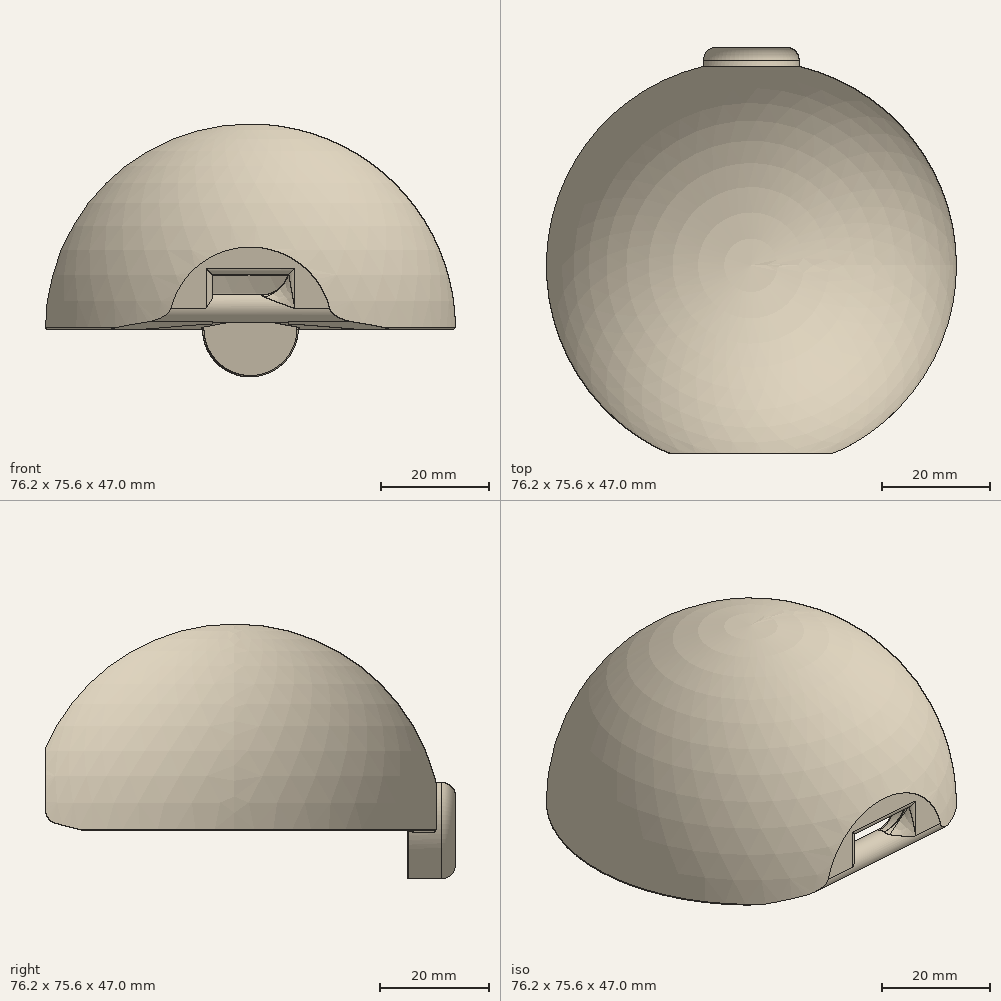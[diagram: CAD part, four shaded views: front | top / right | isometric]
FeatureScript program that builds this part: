
annotation { "Feature Type Name" : "Feature", "Feature Type Description" : "" }
export const myFeature = defineFeature(function(context is Context, id is Id, definition is map)
    precondition{}
    {
        {
            var Q0;
            Q0=qCreatedBy(makeId("Front.planeOp"),FACE);
            var sketch = newSketch(context, id + "F0", { "sketchPlane" : qUnion([Q0])});
            skArc(sketch, "E0", {"start": v(0, 38.1) * mm, "mid": v(-26.94, 26.94) * mm, "end": v(-38.1, 0) * mm});
            skLineSegment(sketch, "E1", {"start": v(-38.1, 0) * mm, "end": v(-31.75, 0) * mm});
            skArc(sketch, "E2.0", {"start": v(0, 31.75) * mm, "mid": v(-22.45, 22.45) * mm, "end": v(-31.75, 0) * mm});
            skLineSegment(sketch, "E3", {"start": v(0, 38.1) * mm, "end": v(0, 31.75) * mm});
            skSolve(sketch);
        }
        {
            var Q0;
            Q0=makeQuery(id+"F0.imprint","IMPRINT",FACE,{"disambiguationData":[TD([[makeQuery(id+"F0.imprint","IMPRINT",EDGE,{"derivedFrom":sQuery(id+"F0.wireOp",EDGE,"E0")}),1.0]])]});
            var Q1;
            Q1=sQuery(id+"F0.wireOp",EDGE,"E3");
            revolve(context, id + "F1", {"entities" : qUnion([Q0]), "axis" : qUnion([Q1]), "revolveType" : RevolveType.FULL});
        }
        {
            var Q0;
            Q0=qCreatedBy(makeId("Front.planeOp"),FACE);
            cPlane(context, id + "F2", {"entities" : qUnion([Q0]), "cplaneType" : CPlaneType.OFFSET, "offset" : 38.1 * mm, "oppositeDirection" : true, "width" : 152.4 * mm, "height" : 152.4 * mm});
        }
        {
            var Q0;
            Q0=qCreatedBy(id+"F2.planeOp",FACE);
            var sketch = newSketch(context, id + "F3", { "sketchPlane" : qUnion([Q0])});
            skCircle(sketch, "E4", {"center": v(0, 0) * mm, "radius": 8.9 * mm});
            skSolve(sketch);
        }
        {
            var Q0;
            Q0=makeQuery(id+"F3.imprint","IMPRINT",FACE,{"disambiguationData":[TD([[makeQuery(id+"F3.imprint","IMPRINT",EDGE,{"derivedFrom":sQuery(id+"F3.wireOp",EDGE,"E4")}),1.0]])]});
            extrude(context, id + "F4", {"entities" : qUnion([Q0]), "operationType" : NewBodyOperationType.ADD, "oppositeDirection" : true, "depth" : 2.54 * mm, "hasSecondDirection" : true, "secondDirectionOppositeDirection" : false, "secondDirectionDepth" : 6.35 * mm});
        }
        {
            var Q0;
            Q0=qCreatedBy(makeId("Right.planeOp"),FACE);
            var sketch = newSketch(context, id + "F5", { "sketchPlane" : qUnion([Q0])});
            skPoint(sketch, "E5.0.0.start.orphan", {"position": v(31.75, 0) * mm});
            skLineSegment(sketch, "E6.trimOffspring", {"start": v(-31.75, 0) * mm, "end": v(-38.1, 0) * mm});
            skPoint(sketch, "E5.0.1.start.orphan", {"position": v(37.05, 0) * mm});
            skPoint(sketch, "E5.0.4.end.orphan", {"position": v(31.75, 0) * mm});
            skPoint(sketch, "E5.0.2.end.orphan", {"position": v(37.05, 0) * mm});
            skPoint(sketch, "E5.0.2.start.orphan", {"position": v(31.75, 0) * mm});
            skCircle(sketch, "E7", {"center": v(-32.39, 3.81) * mm, "radius": 2.54 * mm});
            skLineSegment(sketch, "E8", {"start": v(-38.1, 0) * mm, "end": v(-38.1, 6.58) * mm});
            skLineSegment(sketch, "E9", {"start": v(-27.3, 0) * mm, "end": v(-38.1, 0) * mm});
            skArc(sketch, "E10", {"start": v(-27.3, 0) * mm, "mid": v(-29.08, 9.23) * mm, "end": v(-38.1, 6.58) * mm});
            skPoint(sketch, "E11.end.orphan", {"position": v(-21.82, 0) * mm});
            skSolve(sketch);
        }
        {
            var Q0;
            Q0=makeQuery(id+"F5.imprint","IMPRINT",FACE,{"disambiguationData":[TD([[makeQuery(id+"F5.imprint","IMPRINT",EDGE,{"derivedFrom":sQuery(id+"F5.wireOp",EDGE,"E7")}),-1.0]])]});
            extrude(context, id + "F6", {"entities" : qUnion([Q0]), "operationType" : NewBodyOperationType.REMOVE, "oppositeDirection" : true, "depth" : 13.97 * mm, "symmetric" : true});
        }
        {
            var Q0;
            Q0=qCreatedBy(makeId("Right.planeOp"),FACE);
            var sketch = newSketch(context, id + "F7", { "sketchPlane" : qUnion([Q0])});
            skCircle(sketch, "E12.0", {"center": v(-32.39, 3.81) * mm, "radius": 2.54 * mm});
            skLineSegment(sketch, "E13", {"start": v(-34.93, 3.81) * mm, "end": v(-34.93, 18.16) * mm});
            skLineSegment(sketch, "E14", {"start": v(-34.93, 18.16) * mm, "end": v(-42.82, 16.44) * mm});
            skLineSegment(sketch, "E15", {"start": v(-42.82, 16.44) * mm, "end": v(-48.56, -5.7) * mm});
            skLineSegment(sketch, "E16", {"start": v(-48.56, -5.7) * mm, "end": v(-6.3, -5.14) * mm});
            skLineSegment(sketch, "E17", {"start": v(-6.3, -5.14) * mm, "end": v(-27.81, 0) * mm});
            skLineSegment(sketch, "E18", {"start": v(-27.81, 0) * mm, "end": v(-33.02, 1.35) * mm});
            skSolve(sketch);
        }
        {
            var Q0;
            {var subQ0=sQuery(id+"F7.wireOp",EDGE,"E13");Q0=makeQuery(id+"F7.imprint","IMPRINT",FACE,{"disambiguationData":[TD([[makeQuery(id+"F7.imprint","IMPRINT",EDGE,{"derivedFrom":subQ0}),1.0]])]});}
            extrude(context, id + "F8", {"entities" : qUnion([Q0]), "operationType" : NewBodyOperationType.REMOVE, "oppositeDirection" : true, "depth" : 139.7 * mm, "symmetric" : true});
        }
        {
            var Q0;
            Q0=makeQuery(id+"F5.imprint","IMPRINT",FACE,{"disambiguationData":[TD([[makeQuery(id+"F5.imprint","IMPRINT",EDGE,{"derivedFrom":sQuery(id+"F5.wireOp",EDGE,"E7")}),1.0]])]});
            extrude(context, id + "F9", {"entities" : qUnion([Q0]), "operationType" : NewBodyOperationType.ADD, "depth" : 25.4 * mm, "symmetric" : true});
        }
        {
            var Q0;
            Q0=makeQuery(id+"F4.opExtrude","CAP_FACE",FACE,{"disambiguationData":[OSD([sQuery(id+"F3.wireOp",EDGE,"E4")])],"isStart":false});
            var sketch = newSketch(context, id + "F10", { "sketchPlane" : qUnion([Q0])});
            skCircle(sketch, "E19", {"center": v(0, 0) * mm, "radius": 5.08 * mm});
            skSolve(sketch);
        }
        {
            var Q0;
            Q0=makeQuery(id+"F10.imprint","IMPRINT",FACE,{"disambiguationData":[TD([[makeQuery(id+"F10.imprint","IMPRINT",EDGE,{"derivedFrom":sQuery(id+"F10.wireOp",EDGE,"E19")}),1.0]])]});
            extrude(context, id + "F11", {"entities" : qUnion([Q0]), "operationType" : NewBodyOperationType.REMOVE, "oppositeDirection" : true, "depth" : 2.54 * mm});
        }
        {
            var Q0;
            {var subQ0=sQuery(id+"F0.wireOp",EDGE,"E1");var subQ1=sQuery(id+"F0.wireOp",EDGE,"E2.0");Q0=makeQuery(id+"F6.boolean.opBoolean","SPLIT",EDGE,{"disambiguationData":[TD([makeQuery(id+"F6.opExtrude","CAP_FACE",FACE,{"disambiguationData":[OSD([sQuery(id+"F5.wireOp",EDGE,"E7"),sQuery(id+"F5.wireOp",EDGE,"E8"),sQuery(id+"F5.wireOp",EDGE,"E9"),sQuery(id+"F5.wireOp",EDGE,"E10")])],"isStart":true})])],"derivedFrom":makeQuery(id+"F1.opRevolve","SWEPT_EDGE",EDGE,{"disambiguationData":[OSD([subQ0,subQ1])]})});}
            var Q1;
            {var subQ0=sQuery(id+"F0.wireOp",EDGE,"E1");var subQ1=sQuery(id+"F0.wireOp",EDGE,"E2.0");Q1=makeQuery(id+"F6.boolean.opBoolean","SPLIT",EDGE,{"disambiguationData":[TD([makeQuery(id+"F6.opExtrude","CAP_FACE",FACE,{"disambiguationData":[OSD([sQuery(id+"F5.wireOp",EDGE,"E7"),sQuery(id+"F5.wireOp",EDGE,"E8"),sQuery(id+"F5.wireOp",EDGE,"E9"),sQuery(id+"F5.wireOp",EDGE,"E10")])],"isStart":false})])],"derivedFrom":makeQuery(id+"F1.opRevolve","SWEPT_EDGE",EDGE,{"disambiguationData":[OSD([subQ0,subQ1])]})});}
            fillet(context, id + "F12", {"entities" : qUnion([Q0, Q1]), "radius" : 2.54 * mm, "tangentPropagation" : true, "allowEdgeOverflow" : false});
        }
        {
            var Q0;
            Q0=makeQuery(id+"F11.boolean.opBoolean","COPY",EDGE,{"derivedFrom":makeQuery(id+"F11.opExtrude","CAP_EDGE",EDGE,{"disambiguationData":[OSD([sQuery(id+"F10.wireOp",EDGE,"E19")])],"isStart":false})});
            fillet(context, id + "F13", {"entities" : qUnion([Q0]), "radius" : 5.08 * mm, "tangentPropagation" : true, "allowEdgeOverflow" : false});
        }
        {
            var Q0;
            Q0=makeQuery(id+"F13.opFillet","BLEND_EDGE",EDGE,{"blendedFrom":[makeQuery(id+"F11.boolean.opBoolean","COPY",EDGE,{"derivedFrom":makeQuery(id+"F11.opExtrude","CAP_EDGE",EDGE,{"disambiguationData":[OSD([sQuery(id+"F10.wireOp",EDGE,"E19")])],"isStart":false})}),makeQuery(id+"F4.opExtrude","CAP_FACE",FACE,{"disambiguationData":[OSD([sQuery(id+"F3.wireOp",EDGE,"E4")])],"isStart":false})],"blendedInto":[makeQuery(id+"F4.opExtrude","CAP_FACE",FACE,{"disambiguationData":[OSD([sQuery(id+"F3.wireOp",EDGE,"E4")])],"isStart":false})]});
            var Q1;
            Q1=makeQuery(id+"F4.opExtrude","CAP_EDGE",EDGE,{"disambiguationData":[OSD([sQuery(id+"F3.wireOp",EDGE,"E4")])],"isStart":false});
            var Q2;
            {var subQ0=sQuery(id+"F10.wireOp",EDGE,"E19");Q2=makeQuery(id+"F13.opFillet","BLEND_EDGE",EDGE,{"blendedFrom":[makeQuery(id+"F11.boolean.opBoolean","COPY",EDGE,{"derivedFrom":makeQuery(id+"F11.opExtrude","CAP_EDGE",EDGE,{"disambiguationData":[OSD([subQ0])],"isStart":false})}),makeQuery(id+"F11.boolean.opBoolean","COPY",FACE,{"derivedFrom":makeQuery(id+"F11.opExtrude","CAP_FACE",FACE,{"disambiguationData":[OSD([subQ0])],"isStart":false})})],"blendedInto":[makeQuery(id+"F11.boolean.opBoolean","COPY",FACE,{"derivedFrom":makeQuery(id+"F11.opExtrude","CAP_FACE",FACE,{"disambiguationData":[OSD([subQ0])],"isStart":false})})]});}
            fillet(context, id + "F14", {"entities" : qUnion([Q0, Q1, Q2]), "radius" : 2.5 * mm, "tangentPropagation" : true, "allowEdgeOverflow" : false});
        }
        {
            var Q0;
            Q0=makeQuery(id+"F4.boolean.opBoolean","INTERSECT",EDGE,{"disambiguationData":[OD(1.0)],"derivedFrom":[makeQuery(id+"F1.opRevolve","SWEPT_FACE",FACE,{"disambiguationData":[OSD([sQuery(id+"F0.wireOp",EDGE,"E1")])]}),makeQuery(id+"F4.opExtrude","SWEPT_FACE",FACE,{"disambiguationData":[OSD([sQuery(id+"F3.wireOp",EDGE,"E4")])]})]});
            var Q1;
            Q1=makeQuery(id+"F4.boolean.opBoolean","INTERSECT",EDGE,{"disambiguationData":[OD(0.0)],"derivedFrom":[makeQuery(id+"F1.opRevolve","SWEPT_FACE",FACE,{"disambiguationData":[OSD([sQuery(id+"F0.wireOp",EDGE,"E1")])]}),makeQuery(id+"F4.opExtrude","SWEPT_FACE",FACE,{"disambiguationData":[OSD([sQuery(id+"F3.wireOp",EDGE,"E4")])]})]});
            var Q2;
            Q2=makeQuery(id+"F4.boolean.opBoolean","INTERSECT",EDGE,{"disambiguationData":[OD(0.0)],"derivedFrom":[makeQuery(id+"F1.opRevolve","SWEPT_FACE",FACE,{"disambiguationData":[OSD([sQuery(id+"F0.wireOp",EDGE,"E1")])]}),makeQuery(id+"F4.opExtrude","CAP_FACE",FACE,{"disambiguationData":[OSD([sQuery(id+"F3.wireOp",EDGE,"E4")])],"isStart":true})]});
            var Q3;
            Q3=makeQuery(id+"F4.boolean.opBoolean","INTERSECT",EDGE,{"disambiguationData":[OD(1.0)],"derivedFrom":[makeQuery(id+"F1.opRevolve","SWEPT_FACE",FACE,{"disambiguationData":[OSD([sQuery(id+"F0.wireOp",EDGE,"E1")])]}),makeQuery(id+"F4.opExtrude","CAP_FACE",FACE,{"disambiguationData":[OSD([sQuery(id+"F3.wireOp",EDGE,"E4")])],"isStart":true})]});
            fillet(context, id + "F15", {"entities" : qUnion([Q0, Q1, Q2, Q3]), "radius" : 0.25 * mm, "tangentPropagation" : true, "allowEdgeOverflow" : false});
        }
        {
            var Q0;
            {var subQ0=sQuery(id+"F0.wireOp",EDGE,"E0");var subQ1=sQuery(id+"F0.wireOp",EDGE,"E1");Q0=makeQuery(id+"F6.boolean.opBoolean","SPLIT",EDGE,{"disambiguationData":[TD([makeQuery(id+"F6.opExtrude","CAP_FACE",FACE,{"disambiguationData":[OSD([sQuery(id+"F5.wireOp",EDGE,"E7"),sQuery(id+"F5.wireOp",EDGE,"E8"),sQuery(id+"F5.wireOp",EDGE,"E9"),sQuery(id+"F5.wireOp",EDGE,"E10")])],"isStart":false})])],"derivedFrom":makeQuery(id+"F1.opRevolve","SWEPT_EDGE",EDGE,{"disambiguationData":[OSD([subQ0,subQ1])]})});}
            var Q1;
            {var subQ0=sQuery(id+"F0.wireOp",EDGE,"E0");var subQ1=sQuery(id+"F0.wireOp",EDGE,"E1");Q1=makeQuery(id+"F6.boolean.opBoolean","SPLIT",EDGE,{"disambiguationData":[TD([makeQuery(id+"F6.opExtrude","CAP_FACE",FACE,{"disambiguationData":[OSD([sQuery(id+"F5.wireOp",EDGE,"E7"),sQuery(id+"F5.wireOp",EDGE,"E8"),sQuery(id+"F5.wireOp",EDGE,"E9"),sQuery(id+"F5.wireOp",EDGE,"E10")])],"isStart":true})])],"derivedFrom":makeQuery(id+"F1.opRevolve","SWEPT_EDGE",EDGE,{"disambiguationData":[OSD([subQ0,subQ1])]})});}
            fillet(context, id + "F16", {"entities" : qUnion([Q0, Q1]), "radius" : 0.25 * mm, "tangentPropagation" : true, "allowEdgeOverflow" : false});
        }
        {
            var Q0;
            Q0=makeQuery(id+"F4.opExtrude","CAP_EDGE",EDGE,{"disambiguationData":[OSD([sQuery(id+"F3.wireOp",EDGE,"E4")])],"isStart":true});
            fillet(context, id + "F17", {"entities" : qUnion([Q0]), "radius" : 0.25 * mm, "tangentPropagation" : true, "allowEdgeOverflow" : false});
        }
        {
            var Q0;
            Q0=makeQuery(id+"F6.boolean.opBoolean","INTERSECT",EDGE,{"derivedFrom":[makeQuery(id+"F1.opRevolve","SWEPT_FACE",FACE,{"disambiguationData":[OSD([sQuery(id+"F0.wireOp",EDGE,"E2.0")])]}),makeQuery(id+"F6.opExtrude","SWEPT_FACE",FACE,{"disambiguationData":[OSD([sQuery(id+"F5.wireOp",EDGE,"E10")])]})]});
            var Q1;
            Q1=makeQuery(id+"F6.boolean.opBoolean","INTERSECT",EDGE,{"disambiguationData":[OD(0.0)],"derivedFrom":[makeQuery(id+"F1.opRevolve","SWEPT_FACE",FACE,{"disambiguationData":[OSD([sQuery(id+"F0.wireOp",EDGE,"E2.0")])]}),makeQuery(id+"F6.opExtrude","CAP_FACE",FACE,{"disambiguationData":[OSD([sQuery(id+"F5.wireOp",EDGE,"E7"),sQuery(id+"F5.wireOp",EDGE,"E8"),sQuery(id+"F5.wireOp",EDGE,"E9"),sQuery(id+"F5.wireOp",EDGE,"E10")])],"isStart":true})]});
            var Q2;
            Q2=makeQuery(id+"F8.boolean.opBoolean","INTERSECT",EDGE,{"derivedFrom":[makeQuery(id+"F6.boolean.opBoolean","COPY",FACE,{"derivedFrom":makeQuery(id+"F6.opExtrude","CAP_FACE",FACE,{"disambiguationData":[OSD([sQuery(id+"F5.wireOp",EDGE,"E7"),sQuery(id+"F5.wireOp",EDGE,"E8"),sQuery(id+"F5.wireOp",EDGE,"E9"),sQuery(id+"F5.wireOp",EDGE,"E10")])],"isStart":true})}),makeQuery(id+"F8.opExtrude","SWEPT_FACE",FACE,{"disambiguationData":[OSD([sQuery(id+"F7.wireOp",EDGE,"E13")])]})]});
            var Q3;
            Q3=makeQuery(id+"F8.boolean.opBoolean","INTERSECT",EDGE,{"derivedFrom":[makeQuery(id+"F6.boolean.opBoolean","COPY",FACE,{"derivedFrom":makeQuery(id+"F6.opExtrude","SWEPT_FACE",FACE,{"disambiguationData":[OSD([sQuery(id+"F5.wireOp",EDGE,"E10")])]})}),makeQuery(id+"F8.opExtrude","SWEPT_FACE",FACE,{"disambiguationData":[OSD([sQuery(id+"F7.wireOp",EDGE,"E13")])]})]});
            var Q4;
            Q4=makeQuery(id+"F8.boolean.opBoolean","INTERSECT",EDGE,{"derivedFrom":[makeQuery(id+"F6.boolean.opBoolean","COPY",FACE,{"derivedFrom":makeQuery(id+"F6.opExtrude","CAP_FACE",FACE,{"disambiguationData":[OSD([sQuery(id+"F5.wireOp",EDGE,"E7"),sQuery(id+"F5.wireOp",EDGE,"E8"),sQuery(id+"F5.wireOp",EDGE,"E9"),sQuery(id+"F5.wireOp",EDGE,"E10")])],"isStart":false})}),makeQuery(id+"F8.opExtrude","SWEPT_FACE",FACE,{"disambiguationData":[OSD([sQuery(id+"F7.wireOp",EDGE,"E13")])]})]});
            var Q5;
            Q5=makeQuery(id+"F8.boolean.opBoolean","INTERSECT",EDGE,{"disambiguationData":[OD(0.0)],"derivedFrom":[makeQuery(id+"F1.opRevolve","SWEPT_FACE",FACE,{"disambiguationData":[OSD([sQuery(id+"F0.wireOp",EDGE,"E2.0")])]}),makeQuery(id+"F8.opExtrude","SWEPT_FACE",FACE,{"disambiguationData":[OSD([sQuery(id+"F7.wireOp",EDGE,"E18")])]})]});
            fillet(context, id + "F18", {"entities" : qUnion([Q0, Q1, Q2, Q3, Q4, Q5]), "radius" : 1.27 * mm, "tangentPropagation" : true, "allowEdgeOverflow" : false});
        }
        {
            var Q0;
            Q0=makeQuery(id+"F9.boolean.opBoolean","INTERSECT",EDGE,{"disambiguationData":[OD(1.0)],"derivedFrom":[makeQuery(id+"F1.opRevolve","SWEPT_FACE",FACE,{"disambiguationData":[OSD([sQuery(id+"F0.wireOp",EDGE,"E2.0")])]}),makeQuery(id+"F9.opExtrude","SWEPT_FACE",FACE,{"disambiguationData":[OSD([sQuery(id+"F5.wireOp",EDGE,"E7")])]})]});
            var Q1;
            Q1=makeQuery(id+"F9.boolean.opBoolean","INTERSECT",EDGE,{"disambiguationData":[OD(0.0)],"derivedFrom":[makeQuery(id+"F1.opRevolve","SWEPT_FACE",FACE,{"disambiguationData":[OSD([sQuery(id+"F0.wireOp",EDGE,"E2.0")])]}),makeQuery(id+"F9.opExtrude","SWEPT_FACE",FACE,{"disambiguationData":[OSD([sQuery(id+"F5.wireOp",EDGE,"E7")])]})]});
            fillet(context, id + "F19", {"entities" : qUnion([Q0, Q1]), "radius" : 5.08 * mm, "tangentPropagation" : true, "allowEdgeOverflow" : false});
        }
    });
